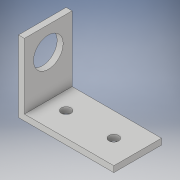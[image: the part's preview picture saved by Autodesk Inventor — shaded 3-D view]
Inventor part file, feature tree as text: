
AUTODESK INVENTOR PART (.ipt)
format: ipt  version: 2018 (Build 220112000, 112)  size: 122,368 bytes
history: native  units: in
note: dims shown in document units (in); Inventor stores cm internally (conversion verified against a paired STEP export)
features: extrude x3, sketch x3
ambient origin geometry x8: Origin, YZ Plane, XZ Plane, XY Plane, X Axis, Y Axis, Z Axis, Center Point
bodies: Solid1 (feature_tree)
feature tree (6):
  extrude  "Extrusion1"  Depth=1.5in
  extrude  "Extrusion2"  Depth=0.125in
  extrude  "Extrusion4"  Depth=1.0in
  sketch  "Sketch1"  dims[d0=0.125in d1=1.5in]
  sketch  "Sketch2"  dims[d2=2.0in d3=0.125in]
  sketch  "Sketch3"  dims[d4=1.0in d5=0.0in d6=1.0in d7=0.6225in d8=1.0in d9=0.0in d10=0.5in d11=180.0deg d12=0.2031in d15=1.0in d16=1.0in d17=0.0in]
